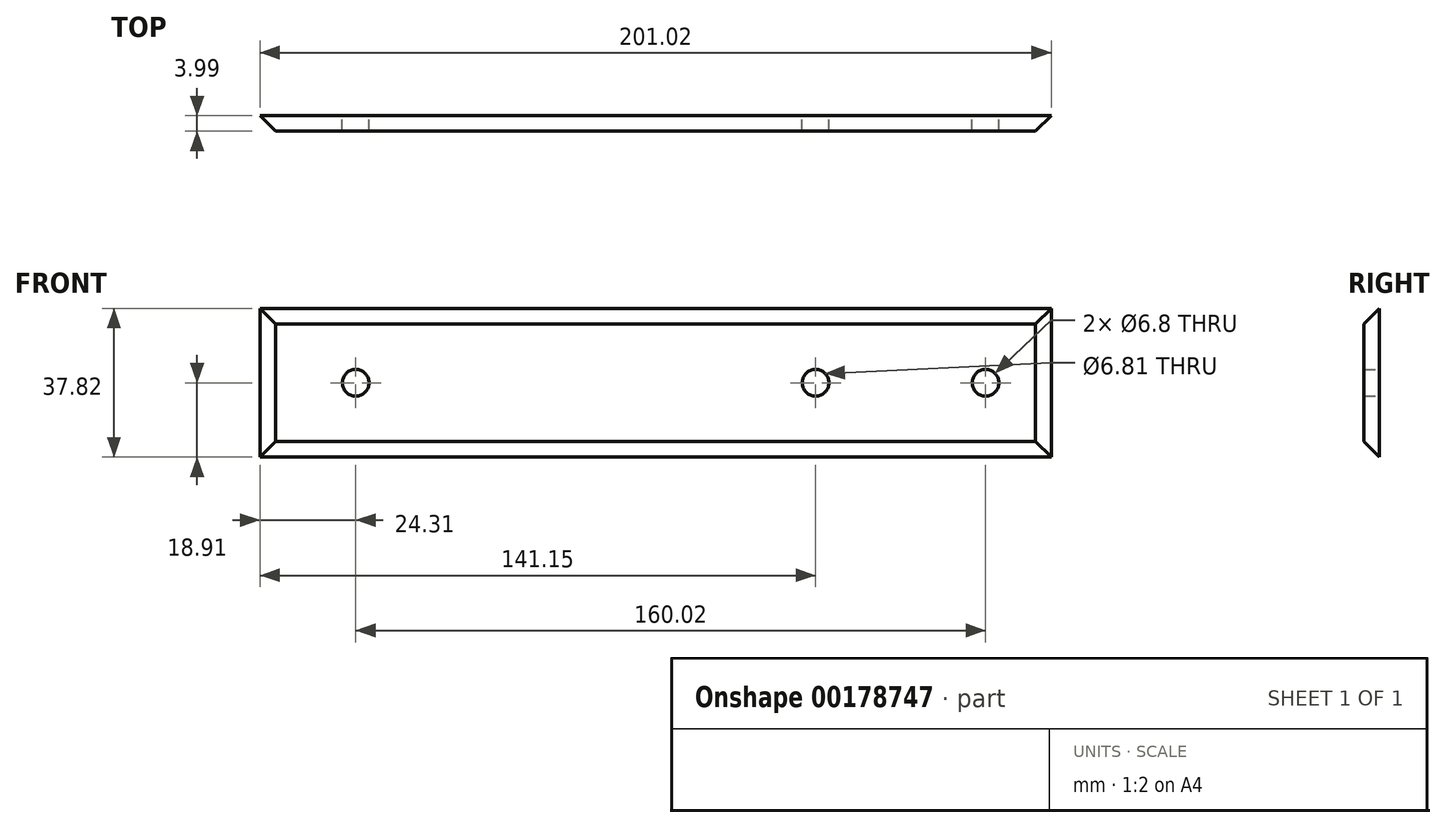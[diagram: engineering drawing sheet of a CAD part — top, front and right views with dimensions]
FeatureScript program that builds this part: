
annotation { "Feature Type Name" : "Feature", "Feature Type Description" : "" }
export const myFeature = defineFeature(function(context is Context, id is Id, definition is map)
    precondition{}
    {
        {
            var Q0;
            Q0=qCreatedBy(makeId("Front.planeOp"),FACE);
            var sketch = newSketch(context, id + "F0", { "sketchPlane" : qUnion([Q0])});
            skLineSegment(sketch, "E0.bottom", {"start": v(101.6, -20) * mm, "end": v(0, -20) * mm});
            skLineSegment(sketch, "E0.top", {"start": v(101.6, 20) * mm, "end": v(0, 20) * mm});
            skLineSegment(sketch, "E0.left", {"start": v(101.6, -20) * mm, "end": v(101.6, 20) * mm});
            skLineSegment(sketch, "E0.right", {"start": v(-101.6, -20) * mm, "end": v(-101.6, 20) * mm});
            skPoint(sketch, "E0.middle", {"position": v(0, 0) * mm});
            skLineSegment(sketch, "E1", {"start": v(101.6, 0) * mm, "end": v(87.22, 0) * mm});
            skCircle(sketch, "E2", {"center": v(83.82, 0) * mm, "radius": 3.4 * mm});
            skCircle(sketch, "E3", {"center": v(-76.2, 0) * mm, "radius": 3.4 * mm});
            skLineSegment(sketch, "E4.trimOffspring", {"start": v(-79.6, 0) * mm, "end": v(-101.6, 0) * mm});
            skLineSegment(sketch, "E5.trimOffspring", {"start": v(80.42, 0) * mm, "end": v(44.04, 0) * mm});
            skCircle(sketch, "E6", {"center": v(40.64, 0) * mm, "radius": 3.4 * mm});
            skLineSegment(sketch, "E7.trimOffspring", {"start": v(37.24, 0) * mm, "end": v(0, 0) * mm});
            skLineSegment(sketch, "E8", {"start": v(0, 0) * mm, "end": v(0, 20) * mm});
            skLineSegment(sketch, "E9", {"start": v(0, 20) * mm, "end": v(0, -20) * mm});
            skLineSegment(sketch, "E10", {"start": v(0, 20) * mm, "end": v(-101.6, 20) * mm});
            skLineSegment(sketch, "E11", {"start": v(0, -20) * mm, "end": v(-101.6, -20) * mm});
            skSolve(sketch);
        }
        {
            var Q0;
            Q0 = qSketchRegion(id + "F0", true);
            extrude(context, id + "F1", {"entities" : qUnion([Q0]), "depth" : 4 * mm});
        }
        {
            var Q0;
            Q0=makeQuery(id+"F1.opExtrude","CAP_EDGE",EDGE,{"disambiguationData":[OSD([sQuery(id+"F0.wireOp",EDGE,"E0.top")])],"isStart":false});
            var Q1;
            Q1=makeQuery(id+"F1.opExtrude","CAP_EDGE",EDGE,{"disambiguationData":[OSD([sQuery(id+"F0.wireOp",EDGE,"E0.right")])],"isStart":false});
            var Q2;
            Q2=makeQuery(id+"F1.opExtrude","CAP_EDGE",EDGE,{"disambiguationData":[OSD([sQuery(id+"F0.wireOp",EDGE,"E0.bottom")])],"isStart":false});
            var Q3;
            Q3=makeQuery(id+"F1.opExtrude","CAP_EDGE",EDGE,{"disambiguationData":[OSD([sQuery(id+"F0.wireOp",EDGE,"E0.left")])],"isStart":false});
            chamfer(context, id + "F2", {"entities" : qUnion([Q0, Q1, Q2, Q3]), "width" : 5.08 * mm, "tangentPropagation" : true});
        }
    });
